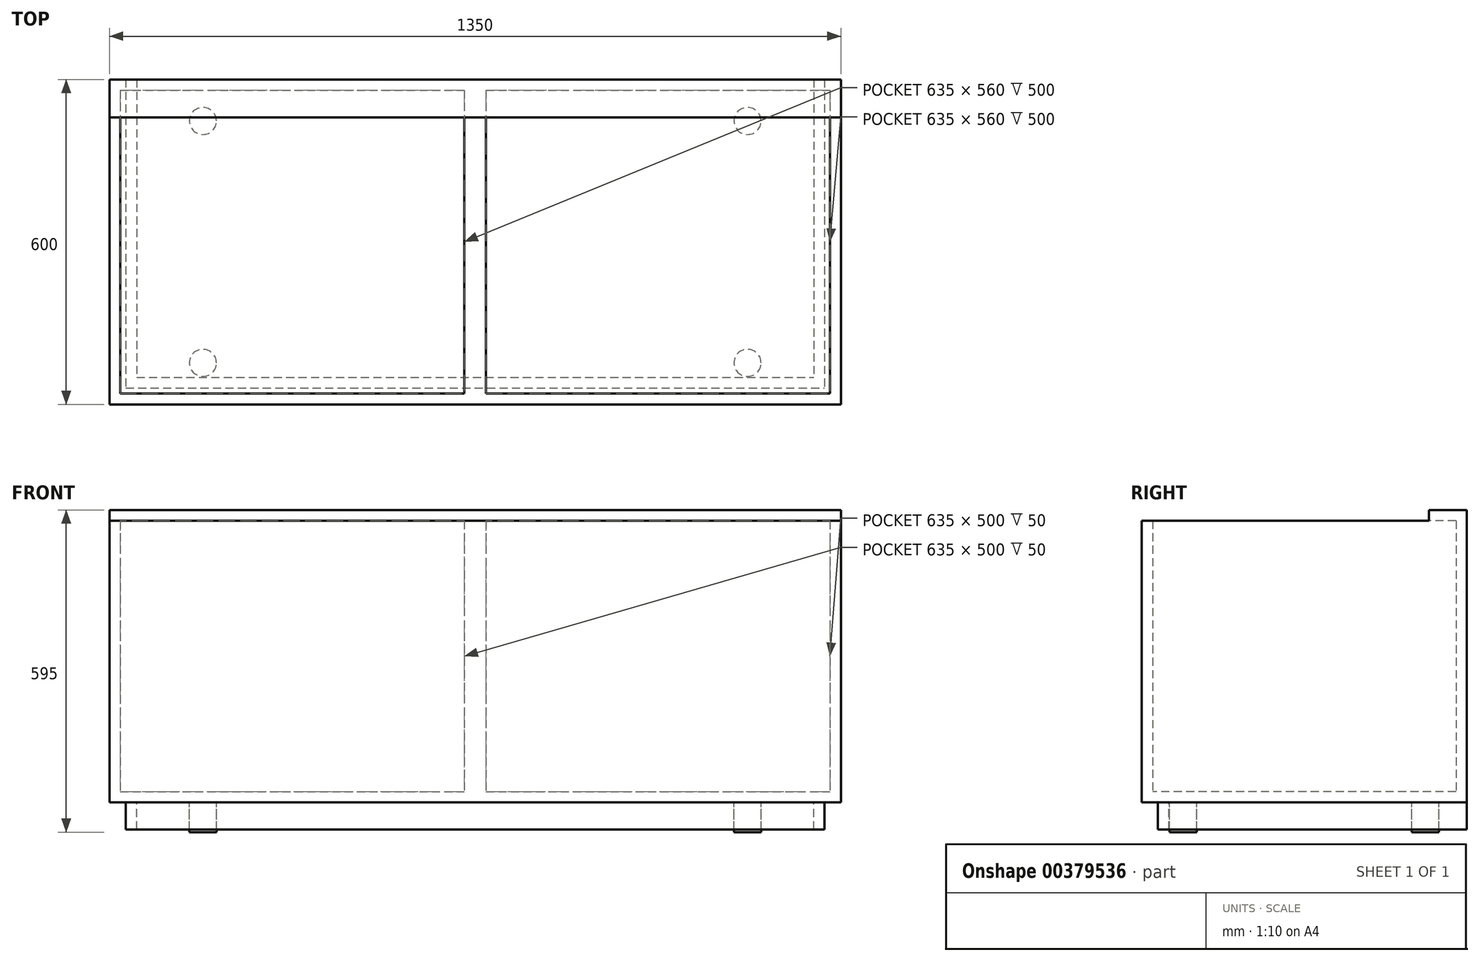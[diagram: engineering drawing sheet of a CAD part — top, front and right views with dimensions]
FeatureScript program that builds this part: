
annotation { "Feature Type Name" : "Feature", "Feature Type Description" : "" }
export const myFeature = defineFeature(function(context is Context, id is Id, definition is map)
    precondition{}
    {
        {
            var Q0;
            Q0=qCreatedBy(makeId("Top.planeOp"),FACE);
            var sketch = newSketch(context, id + "F0", { "sketchPlane" : qUnion([Q0])});
            skLineSegment(sketch, "E0.bottom", {"start": v(-655, 280) * mm, "end": v(655, 280) * mm});
            skLineSegment(sketch, "E0.top", {"start": v(-655, -280) * mm, "end": v(655, -280) * mm});
            skLineSegment(sketch, "E0.left", {"start": v(-655, 280) * mm, "end": v(-655, -280) * mm});
            skLineSegment(sketch, "E0.right", {"start": v(655, 280) * mm, "end": v(655, -280) * mm});
            skPoint(sketch, "E0.middle", {"position": v(0, 0) * mm});
            skLineSegment(sketch, "E1.bottom", {"start": v(-675, 300) * mm, "end": v(675, 300) * mm});
            skLineSegment(sketch, "E1.top", {"start": v(-675, -300) * mm, "end": v(675, -300) * mm});
            skLineSegment(sketch, "E1.left", {"start": v(-675, 300) * mm, "end": v(-675, -300) * mm});
            skLineSegment(sketch, "E1.right", {"start": v(675, 300) * mm, "end": v(675, -300) * mm});
            skLineSegment(sketch, "E2.bottom", {"start": v(-20, 280) * mm, "end": v(20, 280) * mm});
            skLineSegment(sketch, "E2.top", {"start": v(-20, -280) * mm, "end": v(20, -280) * mm});
            skLineSegment(sketch, "E2.left", {"start": v(-20, 280) * mm, "end": v(-20, -280) * mm});
            skLineSegment(sketch, "E2.right", {"start": v(20, 280) * mm, "end": v(20, -280) * mm});
            skLineSegment(sketch, "E3", {"start": v(0, 280) * mm, "end": v(0, -280) * mm});
            skSolve(sketch);
        }
        {
            var Q0;
            Q0=makeQuery(id+"F0.imprint","IMPRINT",FACE,{"disambiguationData":[TD([[makeQuery(id+"F0.imprint","IMPRINT",EDGE,{"derivedFrom":sQuery(id+"F0.wireOp",EDGE,"E0.bottom")}),1.0]])]});
            var Q1;
            {var subQ0=sQuery(id+"F0.wireOp",EDGE,"E2.right");Q1=makeQuery(id+"F0.imprint","IMPRINT",FACE,{"disambiguationData":[TD([[makeQuery(id+"F0.imprint","IMPRINT",EDGE,{"derivedFrom":subQ0}),-1.0]])]});}
            var Q2;
            {var subQ0=sQuery(id+"F0.wireOp",EDGE,"E2.left");Q2=makeQuery(id+"F0.imprint","IMPRINT",FACE,{"disambiguationData":[TD([[makeQuery(id+"F0.imprint","IMPRINT",EDGE,{"derivedFrom":subQ0}),1.0]])]});}
            extrude(context, id + "F1", {"entities" : qUnion([Q0, Q1, Q2]), "depth" : 500 * mm});
        }
        {
            var Q0;
            Q0=makeQuery(id+"F1.opExtrude","CAP_FACE",FACE,{"disambiguationData":[OSD([sQuery(id+"F0.wireOp",EDGE,"E0.bottom"),sQuery(id+"F0.wireOp",EDGE,"E0.top"),sQuery(id+"F0.wireOp",EDGE,"E0.left"),sQuery(id+"F0.wireOp",EDGE,"E0.right"),sQuery(id+"F0.wireOp",EDGE,"E1.bottom"),sQuery(id+"F0.wireOp",EDGE,"E1.top"),sQuery(id+"F0.wireOp",EDGE,"E1.left"),sQuery(id+"F0.wireOp",EDGE,"E1.right")])],"isStart":false});
            var sketch = newSketch(context, id + "F2", { "sketchPlane" : qUnion([Q0])});
            skLineSegment(sketch, "E4.bottom", {"start": v(-675, 300) * mm, "end": v(675, 300) * mm});
            skLineSegment(sketch, "E4.top", {"start": v(-675, 230) * mm, "end": v(675, 230) * mm});
            skLineSegment(sketch, "E4.left", {"start": v(-675, 300) * mm, "end": v(-675, 230) * mm});
            skLineSegment(sketch, "E4.right", {"start": v(675, 300) * mm, "end": v(675, 230) * mm});
            skSolve(sketch);
        }
        {
            var Q0;
            Q0 = qSketchRegion(id + "F2", true);
            extrude(context, id + "F3", {"entities" : qUnion([Q0]), "operationType" : NewBodyOperationType.ADD, "depth" : 20 * mm});
        }
        {
            var Q0;
            Q0=makeQuery(id+"F1.opExtrude","CAP_FACE",FACE,{"disambiguationData":[OSD([sQuery(id+"F0.wireOp",EDGE,"E0.bottom"),sQuery(id+"F0.wireOp",EDGE,"E0.top"),sQuery(id+"F0.wireOp",EDGE,"E0.left"),sQuery(id+"F0.wireOp",EDGE,"E0.right"),sQuery(id+"F0.wireOp",EDGE,"E1.bottom"),sQuery(id+"F0.wireOp",EDGE,"E1.top"),sQuery(id+"F0.wireOp",EDGE,"E1.left"),sQuery(id+"F0.wireOp",EDGE,"E1.right")])],"isStart":true});
            var sketch = newSketch(context, id + "F4", { "sketchPlane" : qUnion([Q0])});
            skLineSegment(sketch, "E5.bottom", {"start": v(-675, 300) * mm, "end": v(675, 300) * mm});
            skLineSegment(sketch, "E5.top", {"start": v(-675, -300) * mm, "end": v(675, -300) * mm});
            skLineSegment(sketch, "E5.left", {"start": v(-675, 300) * mm, "end": v(-675, -300) * mm});
            skLineSegment(sketch, "E5.right", {"start": v(675, 300) * mm, "end": v(675, -300) * mm});
            skSolve(sketch);
        }
        {
            var Q0;
            Q0 = qSketchRegion(id + "F4", true);
            extrude(context, id + "F5", {"entities" : qUnion([Q0]), "operationType" : NewBodyOperationType.ADD, "depth" : 20 * mm});
        }
        {
            var Q0;
            Q0=makeQuery(id+"F5.opExtrude","CAP_FACE",FACE,{"disambiguationData":[OSD([sQuery(id+"F4.wireOp",EDGE,"E5.bottom"),sQuery(id+"F4.wireOp",EDGE,"E5.top"),sQuery(id+"F4.wireOp",EDGE,"E5.left"),sQuery(id+"F4.wireOp",EDGE,"E5.right")])],"isStart":false});
            var sketch = newSketch(context, id + "F6", { "sketchPlane" : qUnion([Q0])});
            skLineSegment(sketch, "E6", {"start": v(-675, 300) * mm, "end": v(675, -300) * mm, "construction": true});
            skLineSegment(sketch, "E7", {"start": v(675, 300) * mm, "end": v(-675, -300) * mm, "construction": true});
            skLineSegment(sketch, "E8", {"start": v(0, 300) * mm, "end": v(-675, 0) * mm, "construction": true});
            skLineSegment(sketch, "E9", {"start": v(-675, 0) * mm, "end": v(675, 0) * mm, "construction": true});
            skLineSegment(sketch, "E10", {"start": v(675, 0) * mm, "end": v(0, 300) * mm, "construction": true});
            skLineSegment(sketch, "E11", {"start": v(-675, 0) * mm, "end": v(0, -300) * mm, "construction": true});
            skLineSegment(sketch, "E12", {"start": v(0, -300) * mm, "end": v(675, 0) * mm, "construction": true});
            skLineSegment(sketch, "E13", {"start": v(675, -150) * mm, "end": v(-675, -150) * mm, "construction": true});
            skPoint(sketch, "E13.startSnap0", {"position": v(337.5, -150) * mm});
            skLineSegment(sketch, "E14", {"start": v(-675, 150) * mm, "end": v(675, 150) * mm, "construction": true});
            skPoint(sketch, "E14.startSnap0", {"position": v(-337.5, 150) * mm});
            skCircle(sketch, "E15", {"center": v(0, 0) * mm, "radius": 550 * mm, "construction": true});
            skCircle(sketch, "E16", {"center": v(-502.6, 223.38) * mm, "radius": 25 * mm});
            skCircle(sketch, "E17", {"center": v(-502.6, -223.38) * mm, "radius": 25 * mm});
            skCircle(sketch, "E18", {"center": v(502.6, 223.38) * mm, "radius": 25 * mm});
            skCircle(sketch, "E19", {"center": v(502.6, -223.38) * mm, "radius": 25 * mm});
            skSolve(sketch);
        }
        {
            var Q0;
            Q0=makeQuery(id+"F6.imprint","IMPRINT",FACE,{"disambiguationData":[TD([[makeQuery(id+"F6.imprint","IMPRINT",EDGE,{"derivedFrom":sQuery(id+"F6.wireOp",EDGE,"E16")}),1.0]])]});
            var Q1;
            Q1=makeQuery(id+"F6.imprint","IMPRINT",FACE,{"disambiguationData":[TD([[makeQuery(id+"F6.imprint","IMPRINT",EDGE,{"derivedFrom":sQuery(id+"F6.wireOp",EDGE,"E17")}),1.0]])]});
            var Q2;
            Q2=makeQuery(id+"F6.imprint","IMPRINT",FACE,{"disambiguationData":[TD([[makeQuery(id+"F6.imprint","IMPRINT",EDGE,{"derivedFrom":sQuery(id+"F6.wireOp",EDGE,"E19")}),1.0]])]});
            var Q3;
            Q3=makeQuery(id+"F6.imprint","IMPRINT",FACE,{"disambiguationData":[TD([[makeQuery(id+"F6.imprint","IMPRINT",EDGE,{"derivedFrom":sQuery(id+"F6.wireOp",EDGE,"E18")}),1.0]])]});
            extrude(context, id + "F7", {"entities" : qUnion([Q0, Q1, Q2, Q3]), "operationType" : NewBodyOperationType.ADD, "depth" : 55 * mm});
        }
        {
            var Q0;
            Q0=makeQuery(id+"F5.opExtrude","CAP_FACE",FACE,{"disambiguationData":[OSD([sQuery(id+"F4.wireOp",EDGE,"E5.bottom"),sQuery(id+"F4.wireOp",EDGE,"E5.top"),sQuery(id+"F4.wireOp",EDGE,"E5.left"),sQuery(id+"F4.wireOp",EDGE,"E5.right")])],"isStart":false});
            var sketch = newSketch(context, id + "F8", { "sketchPlane" : qUnion([Q0])});
            skLineSegment(sketch, "E20.top", {"start": v(-645, 270) * mm, "end": v(645, 270) * mm});
            skLineSegment(sketch, "E20.left", {"start": v(-645, -270) * mm, "end": v(-645, 270) * mm});
            skLineSegment(sketch, "E20.right", {"start": v(645, -270) * mm, "end": v(645, 270) * mm});
            skPoint(sketch, "E20.middle", {"position": v(0, 0) * mm});
            skLineSegment(sketch, "E21.top", {"start": v(-625, 250) * mm, "end": v(625, 250) * mm});
            skLineSegment(sketch, "E21.left", {"start": v(-625, -250) * mm, "end": v(-625, 250) * mm});
            skLineSegment(sketch, "E21.right", {"start": v(625, -250) * mm, "end": v(625, 250) * mm});
            skLineSegment(sketch, "E22", {"start": v(-645, -270) * mm, "end": v(-645, -300) * mm});
            skLineSegment(sketch, "E23", {"start": v(-625, -300) * mm, "end": v(-625, -250) * mm});
            skLineSegment(sketch, "E24", {"start": v(625, -250) * mm, "end": v(625, -300) * mm});
            skLineSegment(sketch, "E25", {"start": v(645, -300) * mm, "end": v(645, -270) * mm});
            skLineSegment(sketch, "E26", {"start": v(-645, -300) * mm, "end": v(-625, -300) * mm});
            skLineSegment(sketch, "E27", {"start": v(625, -300) * mm, "end": v(645, -300) * mm});
            skSolve(sketch);
        }
        {
            var Q0;
            Q0=makeQuery(id+"F8.imprint","IMPRINT",FACE,{"disambiguationData":[TD([[makeQuery(id+"F8.imprint","IMPRINT",EDGE,{"derivedFrom":sQuery(id+"F8.wireOp",EDGE,"E20.top")}),-1.0]])]});
            extrude(context, id + "F9", {"entities" : qUnion([Q0]), "operationType" : NewBodyOperationType.ADD, "depth" : 50 * mm});
        }
    });
